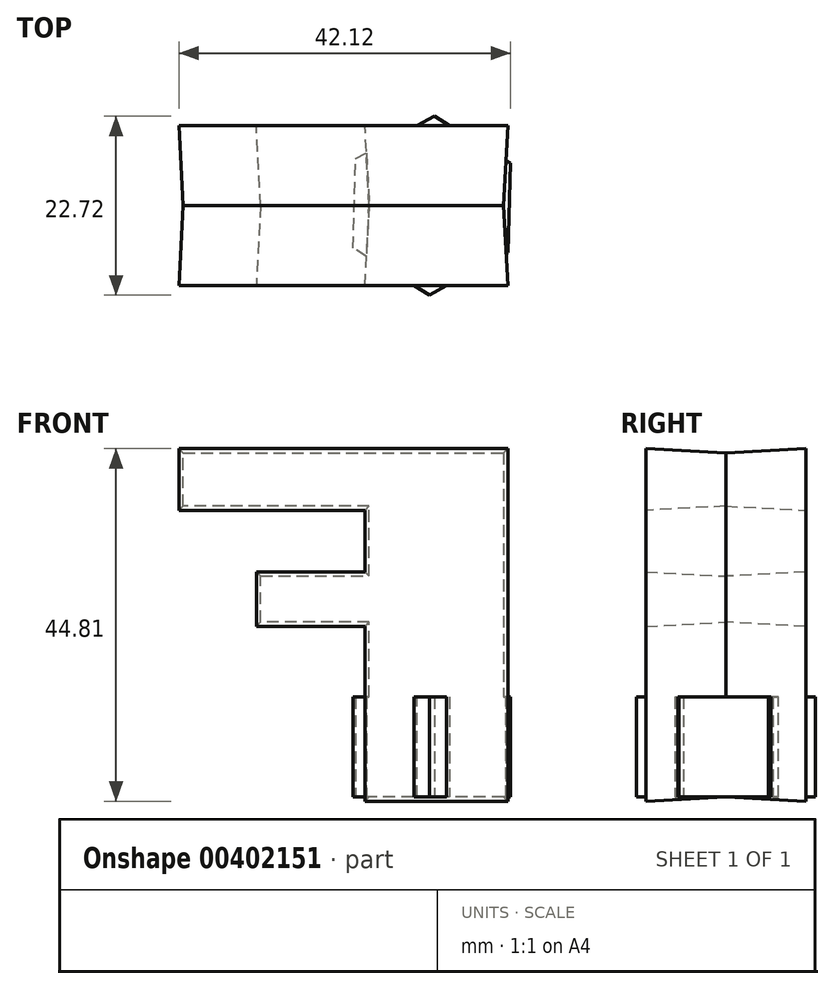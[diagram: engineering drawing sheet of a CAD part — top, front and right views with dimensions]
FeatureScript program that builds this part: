
annotation { "Feature Type Name" : "Feature", "Feature Type Description" : "" }
export const myFeature = defineFeature(function(context is Context, id is Id, definition is map)
    precondition{}
    {
        {
            var Q0;
            Q0=qCreatedBy(makeId("Top.planeOp"),FACE);
            var sketch = newSketch(context, id + "F0", { "sketchPlane" : qUnion([Q0])});
            skCircle(sketch, "E0.cCircle", {"center": v(0, 0) * mm, "radius": 9.84 * mm, "construction": true});
            skLineSegment(sketch, "E0.0", {"start": v(-9.68, 5.95) * mm, "end": v(0.32, 11.36) * mm});
            skLineSegment(sketch, "E0.1", {"start": v(0.32, 11.36) * mm, "end": v(10, 5.4) * mm});
            skLineSegment(sketch, "E0.2", {"start": v(10, 5.4) * mm, "end": v(9.68, -5.95) * mm});
            skLineSegment(sketch, "E0.3", {"start": v(9.68, -5.95) * mm, "end": v(-0.32, -11.36) * mm});
            skLineSegment(sketch, "E0.4", {"start": v(-0.32, -11.36) * mm, "end": v(-10, -5.4) * mm});
            skLineSegment(sketch, "E0.5", {"start": v(-10, -5.4) * mm, "end": v(-9.68, 5.95) * mm});
            skPoint(sketch, "E0.0.midPoint", {"position": v(-4.68, 8.66) * mm});
            skSolve(sketch);
        }
        {
            var Q0;
            Q0 = qSketchRegion(id + "F0", true);
            extrude(context, id + "F1", {"entities" : qUnion([Q0]), "depth" : 12.7 * mm});
        }
        {
            var Q0;
            Q0=qCreatedBy(makeId("Front.planeOp"),FACE);
            var sketch = newSketch(context, id + "F2", { "sketchPlane" : qUnion([Q0])});
            skLineSegment(sketch, "E1.bottom", {"start": v(9.12, 0) * mm, "end": v(-7.95, 0) * mm});
            skLineSegment(sketch, "E1.top", {"start": v(9.12, 43.75) * mm, "end": v(-7.95, 43.75) * mm});
            skLineSegment(sketch, "E1.left", {"start": v(9.12, 0) * mm, "end": v(9.12, 43.75) * mm});
            skLineSegment(sketch, "E1.right", {"start": v(-7.95, 0) * mm, "end": v(-7.95, 43.75) * mm});
            skLineSegment(sketch, "E2.bottom", {"start": v(-7.95, 43.75) * mm, "end": v(-31.58, 43.75) * mm});
            skLineSegment(sketch, "E2.top", {"start": v(-7.95, 36.96) * mm, "end": v(-31.58, 36.96) * mm});
            skLineSegment(sketch, "E2.left", {"start": v(-7.95, 43.75) * mm, "end": v(-7.95, 36.96) * mm});
            skLineSegment(sketch, "E2.right", {"start": v(-31.58, 43.75) * mm, "end": v(-31.58, 36.96) * mm});
            skLineSegment(sketch, "E3.bottom", {"start": v(-7.95, 28.07) * mm, "end": v(-21.76, 28.07) * mm});
            skLineSegment(sketch, "E3.top", {"start": v(-7.95, 22.23) * mm, "end": v(-21.76, 22.23) * mm});
            skLineSegment(sketch, "E3.left", {"start": v(-7.95, 28.07) * mm, "end": v(-7.95, 22.23) * mm});
            skLineSegment(sketch, "E3.right", {"start": v(-21.76, 28.07) * mm, "end": v(-21.76, 22.23) * mm});
            skSolve(sketch);
        }
        {
            var Q0;
            Q0 = qSketchRegion(id + "F2", true);
            extrude(context, id + "F3", {"entities" : qUnion([Q0]), "operationType" : NewBodyOperationType.ADD, "depth" : 10.16 * mm, "hasDraft" : true, "draftAngle" : 3 * degree, "hasSecondDirection" : true, "secondDirectionOppositeDirection" : true, "secondDirectionDepth" : 10.16 * mm, "hasSecondDirectionDraft" : true, "secondDirectionDraftAngle" : 3 * degree});
        }
    });
